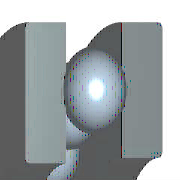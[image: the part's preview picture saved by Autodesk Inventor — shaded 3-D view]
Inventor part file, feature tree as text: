
AUTODESK INVENTOR PART (.ipt)
format: ipt  version: 2022 (Build 260153000, 153)  size: 304,640 bytes
history: native  units: mm (DEFAULTED — no unit token found)
features: sketch x1, other x1, pattern_circular x1
ambient origin geometry x8: Origin, YZ Plane, XZ Plane, XY Plane, X Axis, Y Axis, Z Axis, Center Point
bodies: Solid1 (feature_tree), Body (feature_tree)
feature tree (3):
  sketch  "Sketch"  dims[d0=2.0mm d9=90.0deg d10=90.0deg d1=130.0mm d2=360.0deg d3=4.4mm d4=0.6mm d5=0.6mm d6=0.0mm d7=0.0mm d8=25.0mm d11=25.0mm d12=36.0mm d13=47.0mm d14=47.0mm d15=5.0mm d16=10.0mm d18=3.0mm d19=0.0mm d46=0.0mm d47=0.0mm]
  other  "Ball"
  pattern_circular  "Balls"  Angle=90.0deg  [1 undecoded]
note: 1 required parameter value undecoded (feature->parameter linkage not recoverable at this tier; creation-order binding heuristic only, values carry confidence <= 0.55)
